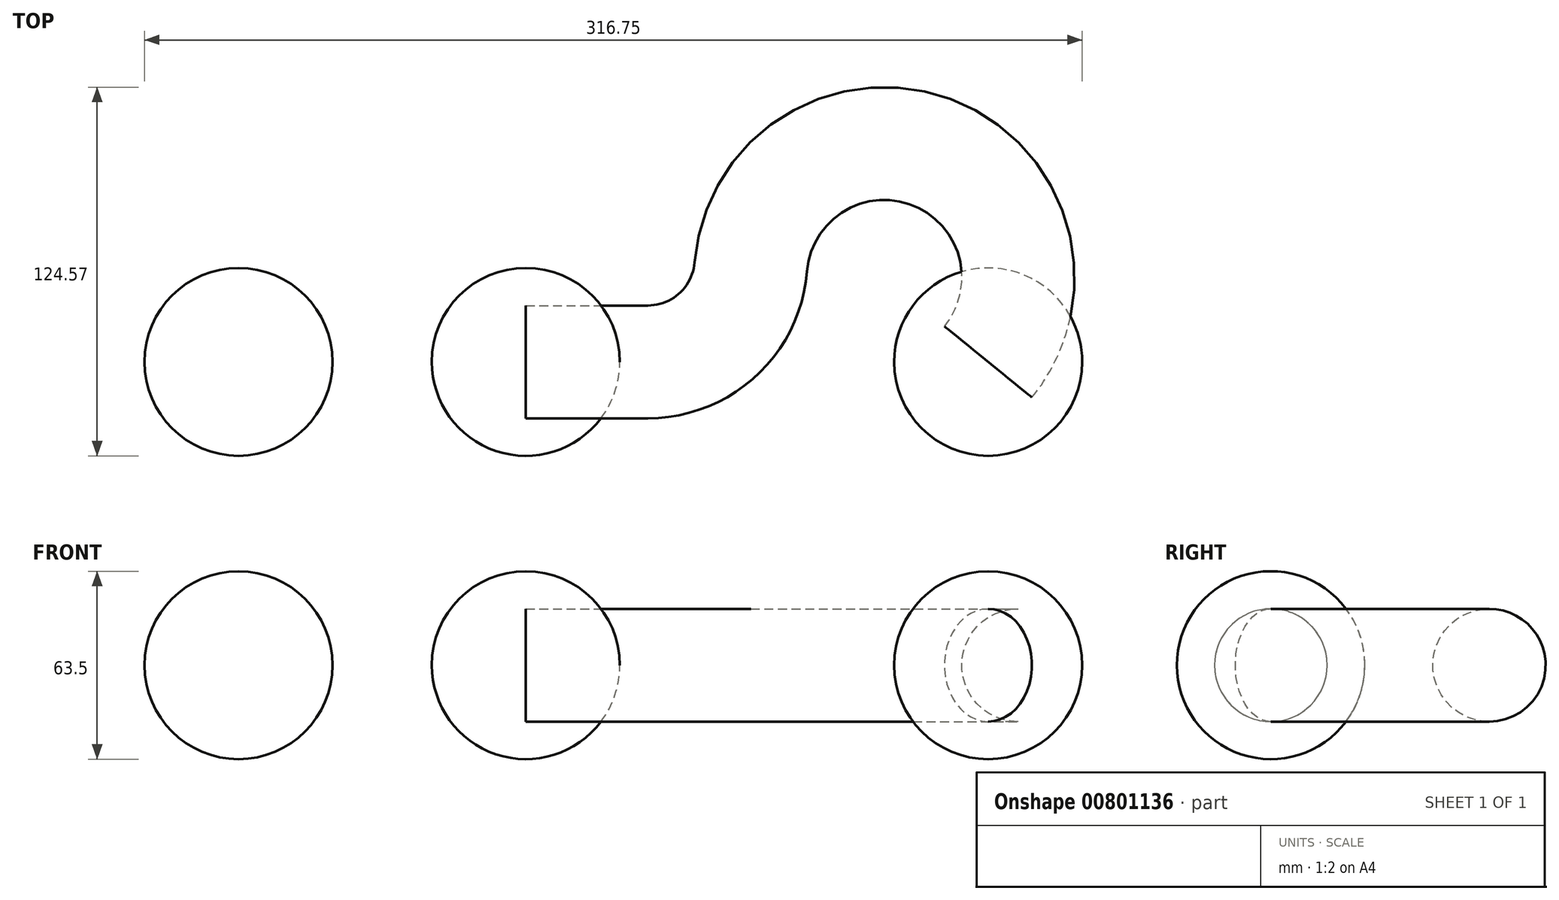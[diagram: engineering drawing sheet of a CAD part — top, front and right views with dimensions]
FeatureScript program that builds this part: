
annotation { "Feature Type Name" : "Feature", "Feature Type Description" : "" }
export const myFeature = defineFeature(function(context is Context, id is Id, definition is map)
    precondition{}
    {
        {
            var Q0;
            Q0=qCreatedBy(makeId("Top.planeOp"),FACE);
            var sketch = newSketch(context, id + "F0", { "sketchPlane" : qUnion([Q0])});
            skCircle(sketch, "E0", {"center": v(0, 0) * mm, "radius": 31.75 * mm});
            skLineSegment(sketch, "E1", {"start": v(-31.75, 0) * mm, "end": v(31.75, 0) * mm});
            skCircle(sketch, "E2", {"center": v(156.2, 0) * mm, "radius": 31.75 * mm});
            skLineSegment(sketch, "E3", {"start": v(124.45, 0) * mm, "end": v(187.95, 0) * mm});
            skSolve(sketch);
        }
        {
            var Q0;
            {var subQ0=sQuery(id+"F0.wireOp",EDGE,"E1");Q0=makeQuery(id+"F0.imprint","IMPRINT",FACE,{"disambiguationData":[TD([[makeQuery(id+"F0.imprint","IMPRINT",EDGE,{"derivedFrom":subQ0}),-1.0]])]});}
            var Q1;
            Q1=sQuery(id+"F0.wireOp",EDGE,"E1");
            revolve(context, id + "F1", {"surfaceOperationType" : NewSurfaceOperationType.NEW, "entities" : qUnion([Q0]), "axis" : qUnion([Q1]), "revolveType" : RevolveType.FULL});
        }
        {
            var Q0;
            {var subQ0=sQuery(id+"F0.wireOp",EDGE,"E3");Q0=makeQuery(id+"F0.imprint","IMPRINT",FACE,{"disambiguationData":[TD([[makeQuery(id+"F0.imprint","IMPRINT",EDGE,{"derivedFrom":subQ0}),-1.0]])]});}
            var Q1;
            Q1=sQuery(id+"F0.wireOp",EDGE,"E3");
            revolve(context, id + "F2", {"surfaceOperationType" : NewSurfaceOperationType.NEW, "entities" : qUnion([Q0]), "axis" : qUnion([Q1]), "revolveType" : RevolveType.FULL});
        }
        {
            var Q0;
            Q0=qCreatedBy(makeId("Right.planeOp"),FACE);
            var sketch = newSketch(context, id + "F3", { "sketchPlane" : qUnion([Q0])});
            skCircle(sketch, "E4", {"center": v(0, 0) * mm, "radius": 19.05 * mm});
            skSolve(sketch);
        }
        {
            var Q0;
            Q0=qCreatedBy(makeId("Top.planeOp"),FACE);
            var sketch = newSketch(context, id + "F4", { "sketchPlane" : qUnion([Q0])});
            skLineSegment(sketch, "E5", {"start": v(0, 0) * mm, "end": v(41.25, 0) * mm});
            skArc(sketch, "E6", {"start": v(41.25, 0) * mm, "mid": v(64.9, 9.25) * mm, "end": v(76, 32.1) * mm});
            skArc(sketch, "E7", {"start": v(76, 32.1) * mm, "mid": v(137.9, 70.53) * mm, "end": v(156.2, 0) * mm});
            skSolve(sketch);
        }
        {
            var Q0;
            Q0 = qSketchRegion(id + "F3", true);
            var Q1;
            Q1 = qConstructionFilter(qBodyType(qCreatedBy(id + "F4" ,EDGE), BodyType.WIRE), ConstructionObject.NO);
            sweep(context, id + "F5", {"profiles" : qUnion([Q0]), "path" : qUnion([Q1])});
        }
        {
            var Q0;
            Q0=qCreatedBy(makeId("Top.planeOp"),FACE);
            var sketch = newSketch(context, id + "F6", { "sketchPlane" : qUnion([Q0])});
            skCircle(sketch, "E8", {"center": v(-97.05, 0) * mm, "radius": 31.75 * mm});
            skLineSegment(sketch, "E9", {"start": v(-97.05, -31.75) * mm, "end": v(-97.05, 31.75) * mm});
            skSolve(sketch);
        }
        {
            var Q0;
            {var subQ0=sQuery(id+"F6.wireOp",EDGE,"E9");Q0=makeQuery(id+"F6.imprint","IMPRINT",FACE,{"disambiguationData":[TD([[makeQuery(id+"F6.imprint","IMPRINT",EDGE,{"derivedFrom":subQ0}),1.0]])]});}
            var Q1;
            Q1=sQuery(id+"F6.wireOp",EDGE,"E9");
            revolve(context, id + "F7", {"surfaceOperationType" : NewSurfaceOperationType.NEW, "entities" : qUnion([Q0]), "axis" : qUnion([Q1]), "revolveType" : RevolveType.FULL});
        }
    });
